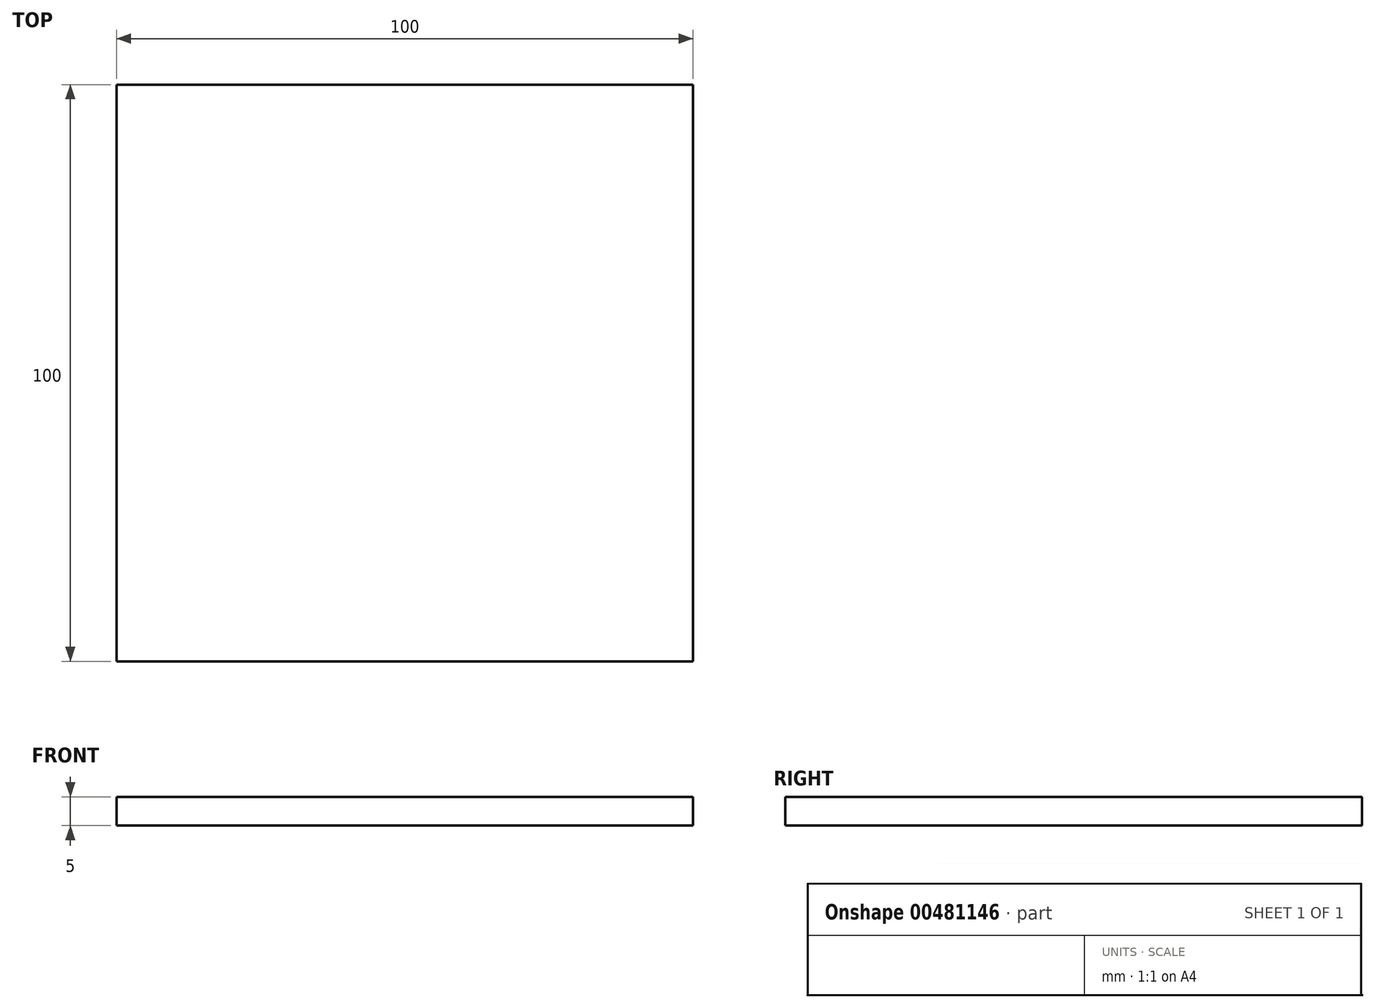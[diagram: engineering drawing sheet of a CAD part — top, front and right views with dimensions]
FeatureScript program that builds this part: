
annotation { "Feature Type Name" : "Feature", "Feature Type Description" : "" }
export const myFeature = defineFeature(function(context is Context, id is Id, definition is map)
    precondition{}
    {
        {
            var Q0;
            Q0=qCreatedBy(makeId("Top.planeOp"),FACE);
            var sketch = newSketch(context, id + "F0", { "sketchPlane" : qUnion([Q0])});
            skLineSegment(sketch, "E0.bottom", {"start": v(-50, 50) * mm, "end": v(50, 50) * mm});
            skLineSegment(sketch, "E0.top", {"start": v(-50, -50) * mm, "end": v(50, -50) * mm});
            skLineSegment(sketch, "E0.left", {"start": v(-50, 50) * mm, "end": v(-50, -50) * mm});
            skLineSegment(sketch, "E0.right", {"start": v(50, 50) * mm, "end": v(50, -50) * mm});
            skPoint(sketch, "E0.middle", {"position": v(0, 0) * mm});
            skSolve(sketch);
        }
        {
            var Q0;
            Q0=makeQuery(id+"F0.imprint","IMPRINT",FACE,{"disambiguationData":[TD([[makeQuery(id+"F0.imprint","IMPRINT",EDGE,{"derivedFrom":sQuery(id+"F0.wireOp",EDGE,"E0.bottom")}),-1.0]])]});
            extrude(context, id + "F1", {"entities" : qUnion([Q0]), "oppositeDirection" : true, "depth" : 5 * mm});
        }
    });
